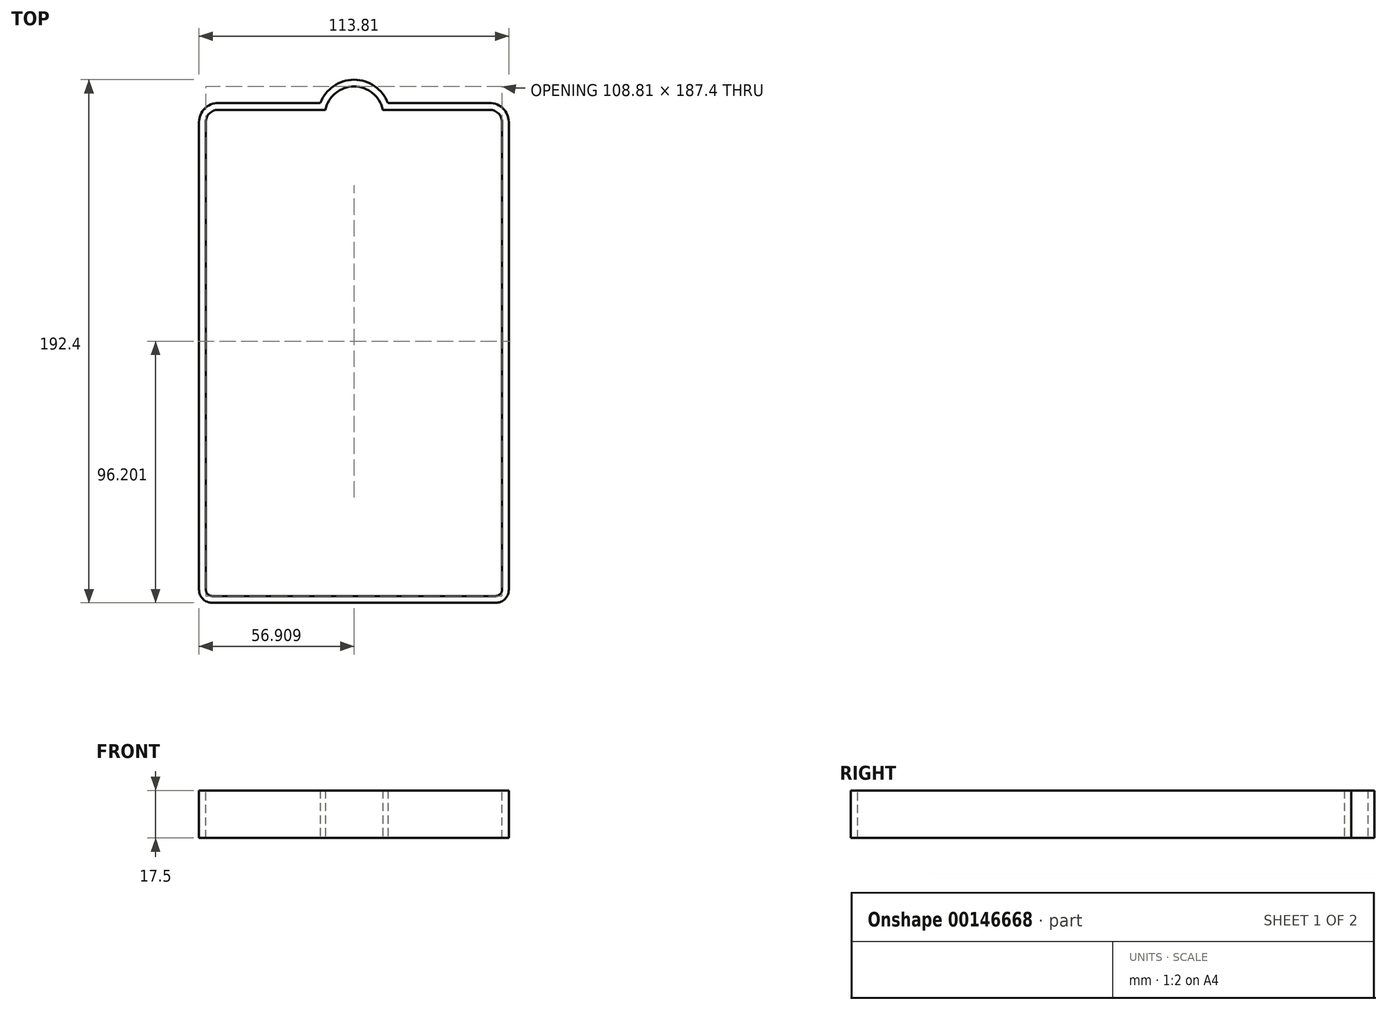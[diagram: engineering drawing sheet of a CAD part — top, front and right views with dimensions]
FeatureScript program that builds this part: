
annotation { "Feature Type Name" : "Feature", "Feature Type Description" : "" }
export const myFeature = defineFeature(function(context is Context, id is Id, definition is map)
    precondition{}
    {
        {
            var Q0;
            Q0=qCreatedBy(makeId("Top.planeOp"),FACE);
            var sketch = newSketch(context, id + "F0", { "sketchPlane" : qUnion([Q0])});
            skLineSegment(sketch, "E0.bottom", {"start": v(-49.76, 88.51) * mm, "end": v(-12.87, 88.51) * mm, "construction": true});
            skLineSegment(sketch, "E0.top", {"start": v(-52.76, -97.3) * mm, "end": v(53.05, -97.3) * mm, "construction": true});
            skLineSegment(sketch, "E0.left", {"start": v(-57.76, 80.51) * mm, "end": v(-57.76, -92.3) * mm, "construction": true});
            skLineSegment(sketch, "E0.right", {"start": v(58.05, 80.51) * mm, "end": v(58.05, -92.3) * mm, "construction": true});
            skArc(sketch, "E1", {"start": v(13.27, 88.51) * mm, "mid": v(0.2, 97.1) * mm, "end": v(-12.87, 88.51) * mm, "construction": true});
            skLineSegment(sketch, "E2.trimOffspring", {"start": v(13.27, 88.51) * mm, "end": v(50.05, 88.51) * mm, "construction": true});
            skPoint(sketch, "E3.visualSharp", {"position": v(-57.76, 88.51) * mm});
            skArc(sketch, "E3.filletArc", {"start": v(-49.76, 88.51) * mm, "mid": v(-55.41, 86.17) * mm, "end": v(-57.76, 80.51) * mm, "construction": true});
            skPoint(sketch, "E4.visualSharp", {"position": v(58.05, 88.51) * mm});
            skArc(sketch, "E4.filletArc", {"start": v(58.05, 80.51) * mm, "mid": v(55.7, 86.17) * mm, "end": v(50.05, 88.51) * mm, "construction": true});
            skPoint(sketch, "E5.visualSharp", {"position": v(-57.76, -97.3) * mm});
            skArc(sketch, "E5.filletArc", {"start": v(-57.76, -92.3) * mm, "mid": v(-56.3, -95.83) * mm, "end": v(-52.76, -97.3) * mm, "construction": true});
            skPoint(sketch, "E6.visualSharp", {"position": v(58.05, -97.3) * mm});
            skArc(sketch, "E6.filletArc", {"start": v(53.05, -97.3) * mm, "mid": v(56.59, -95.83) * mm, "end": v(58.05, -92.3) * mm, "construction": true});
            skArc(sketch, "E7.0", {"start": v(12.6, 87.51) * mm, "mid": v(0.2, 96.1) * mm, "end": v(-12.2, 87.51) * mm});
            skLineSegment(sketch, "E7.1", {"start": v(-49.76, 87.51) * mm, "end": v(-12.2, 87.51) * mm});
            skLineSegment(sketch, "E7.2", {"start": v(12.6, 87.51) * mm, "end": v(50.05, 87.51) * mm});
            skArc(sketch, "E7.3", {"start": v(-49.76, 87.51) * mm, "mid": v(-54.7, 85.46) * mm, "end": v(-56.76, 80.51) * mm});
            skArc(sketch, "E7.4", {"start": v(57.05, 80.51) * mm, "mid": v(55, 85.46) * mm, "end": v(50.05, 87.51) * mm});
            skLineSegment(sketch, "E7.5", {"start": v(57.05, 80.51) * mm, "end": v(57.05, -91.5) * mm});
            skLineSegment(sketch, "E7.6", {"start": v(-51.96, -96.3) * mm, "end": v(52.25, -96.3) * mm});
            skLineSegment(sketch, "E7.7", {"start": v(-56.76, 80.51) * mm, "end": v(-56.76, -91.5) * mm});
            skPoint(sketch, "E8.visualSharp", {"position": v(-56.76, -96.3) * mm});
            skArc(sketch, "E8.filletArc", {"start": v(-56.76, -91.5) * mm, "mid": v(-55.35, -94.9) * mm, "end": v(-51.96, -96.3) * mm});
            skPoint(sketch, "E9.visualSharp", {"position": v(57.05, -96.3) * mm});
            skArc(sketch, "E9.filletArc", {"start": v(52.25, -96.3) * mm, "mid": v(55.65, -94.9) * mm, "end": v(57.05, -91.5) * mm});
            skSolve(sketch);
        }
        {
            var Q0;
            Q0=makeQuery(id+"F0.imprint","IMPRINT",FACE,{"disambiguationData":[TD([[makeQuery(id+"F0.imprint","IMPRINT",EDGE,{"derivedFrom":sQuery(id+"F0.wireOp",EDGE,"E7.0")}),1.0]])]});
            extrude(context, id + "F1", {"entities" : qUnion([Q0]), "depth" : 17.5 * mm});
        }
        {
            var Q0;
            Q0=makeQuery(id+"F1.opExtrude","CAP_FACE",FACE,{"disambiguationData":[OSD([sQuery(id+"F0.wireOp",EDGE,"E7.0"),sQuery(id+"F0.wireOp",EDGE,"E7.1"),sQuery(id+"F0.wireOp",EDGE,"E7.2"),sQuery(id+"F0.wireOp",EDGE,"E7.3"),sQuery(id+"F0.wireOp",EDGE,"E7.4"),sQuery(id+"F0.wireOp",EDGE,"E7.5"),sQuery(id+"F0.wireOp",EDGE,"E7.6"),sQuery(id+"F0.wireOp",EDGE,"E7.7"),sQuery(id+"F0.wireOp",EDGE,"E8.filletArc"),sQuery(id+"F0.wireOp",EDGE,"E9.filletArc")])],"isStart":false});
            var Q1;
            Q1=makeQuery(id+"F1.opExtrude","CAP_FACE",FACE,{"disambiguationData":[OSD([sQuery(id+"F0.wireOp",EDGE,"E7.0"),sQuery(id+"F0.wireOp",EDGE,"E7.1"),sQuery(id+"F0.wireOp",EDGE,"E7.2"),sQuery(id+"F0.wireOp",EDGE,"E7.3"),sQuery(id+"F0.wireOp",EDGE,"E7.4"),sQuery(id+"F0.wireOp",EDGE,"E7.5"),sQuery(id+"F0.wireOp",EDGE,"E7.6"),sQuery(id+"F0.wireOp",EDGE,"E7.7"),sQuery(id+"F0.wireOp",EDGE,"E8.filletArc"),sQuery(id+"F0.wireOp",EDGE,"E9.filletArc")])],"isStart":true});
            shell(context, id + "F2", {"entities" : qUnion([Q0, Q1]), "thickness" : 2.5 * mm});
        }
    });
